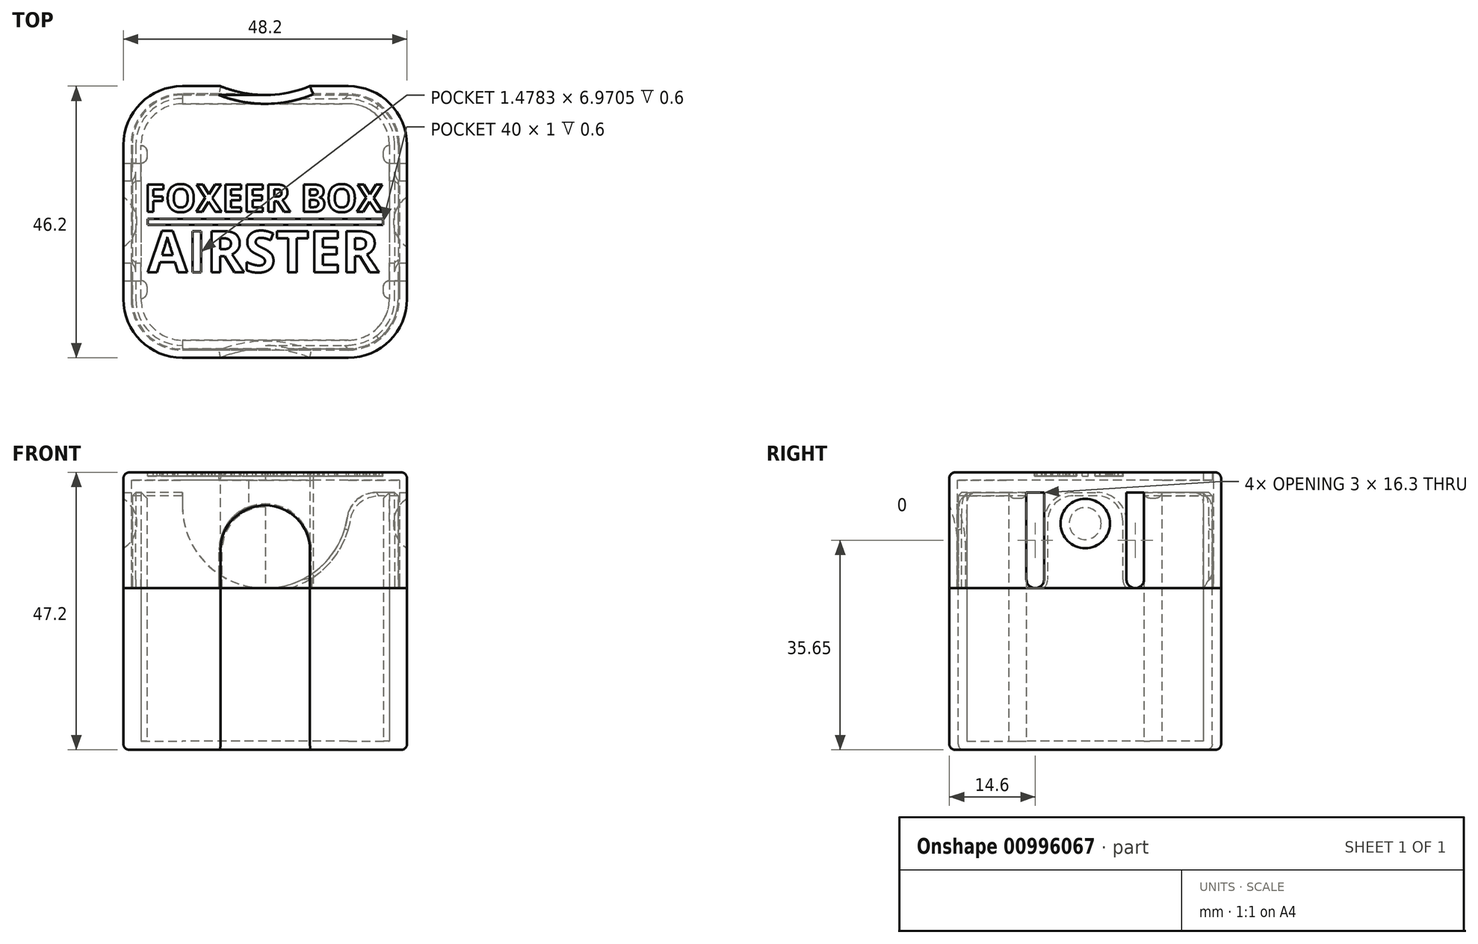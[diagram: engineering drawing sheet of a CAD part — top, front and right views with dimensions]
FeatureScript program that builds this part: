
annotation { "Feature Type Name" : "Feature", "Feature Type Description" : "" }
export const myFeature = defineFeature(function(context is Context, id is Id, definition is map)
    precondition{}
    {
        {
            var Q0;
            Q0=qCreatedBy(makeId("Top.planeOp"),FACE);
            var sketch = newSketch(context, id + "F0", { "sketchPlane" : qUnion([Q0])});
            skLineSegment(sketch, "E0.bottom", {"start": v(14.1, 20.1) * mm, "end": v(-14.1, 20.1) * mm});
            skLineSegment(sketch, "E0.top", {"start": v(14.1, -20.1) * mm, "end": v(-14.1, -20.1) * mm});
            skLineSegment(sketch, "E0.left", {"start": v(21.1, 13.1) * mm, "end": v(21.1, -13.1) * mm});
            skLineSegment(sketch, "E0.right", {"start": v(-21.1, 13.1) * mm, "end": v(-21.1, -13.1) * mm});
            skPoint(sketch, "E0.middle", {"position": v(0, 0) * mm});
            skPoint(sketch, "E1.visualSharp", {"position": v(-21.1, 20.1) * mm});
            skArc(sketch, "E1.filletArc", {"start": v(-14.1, 20.1) * mm, "mid": v(-19.05, 18.05) * mm, "end": v(-21.1, 13.1) * mm});
            skPoint(sketch, "E2.visualSharp", {"position": v(-21.1, -20.1) * mm});
            skArc(sketch, "E2.filletArc", {"start": v(-21.1, -13.1) * mm, "mid": v(-19.05, -18.05) * mm, "end": v(-14.1, -20.1) * mm});
            skPoint(sketch, "E3.visualSharp", {"position": v(21.1, -20.1) * mm});
            skArc(sketch, "E3.filletArc", {"start": v(14.1, -20.1) * mm, "mid": v(19.05, -18.05) * mm, "end": v(21.1, -13.1) * mm});
            skPoint(sketch, "E4.visualSharp", {"position": v(21.1, 20.1) * mm});
            skArc(sketch, "E4.filletArc", {"start": v(21.1, 13.1) * mm, "mid": v(19.05, 18.05) * mm, "end": v(14.1, 20.1) * mm});
            skArc(sketch, "E5.0", {"start": v(22.6, 13.1) * mm, "mid": v(20.11, 19.11) * mm, "end": v(14.1, 21.6) * mm});
            skLineSegment(sketch, "E5.1", {"start": v(14.1, 21.6) * mm, "end": v(-14.1, 21.6) * mm});
            skLineSegment(sketch, "E5.2", {"start": v(22.6, 13.1) * mm, "end": v(22.6, -13.1) * mm});
            skArc(sketch, "E5.3", {"start": v(-14.1, 21.6) * mm, "mid": v(-20.11, 19.11) * mm, "end": v(-22.6, 13.1) * mm});
            skArc(sketch, "E5.4", {"start": v(14.1, -21.6) * mm, "mid": v(20.11, -19.11) * mm, "end": v(22.6, -13.1) * mm});
            skLineSegment(sketch, "E5.5", {"start": v(14.1, -21.6) * mm, "end": v(-14.1, -21.6) * mm});
            skArc(sketch, "E5.6", {"start": v(-22.6, -13.1) * mm, "mid": v(-20.11, -19.11) * mm, "end": v(-14.1, -21.6) * mm});
            skLineSegment(sketch, "E5.7", {"start": v(-22.6, 13.1) * mm, "end": v(-22.6, -13.1) * mm});
            skLineSegment(sketch, "E6.0", {"start": v(24.1, 13.1) * mm, "end": v(24.1, -13.1) * mm});
            skArc(sketch, "E6.1", {"start": v(14.1, -23.1) * mm, "mid": v(21.17, -20.17) * mm, "end": v(24.1, -13.1) * mm});
            skArc(sketch, "E6.2", {"start": v(24.1, 13.1) * mm, "mid": v(21.17, 20.17) * mm, "end": v(14.1, 23.1) * mm});
            skLineSegment(sketch, "E6.3", {"start": v(14.1, -23.1) * mm, "end": v(-14.1, -23.1) * mm});
            skLineSegment(sketch, "E6.4", {"start": v(14.1, 23.1) * mm, "end": v(-14.1, 23.1) * mm});
            skArc(sketch, "E6.5", {"start": v(-14.1, 23.1) * mm, "mid": v(-21.17, 20.17) * mm, "end": v(-24.1, 13.1) * mm});
            skLineSegment(sketch, "E6.6", {"start": v(-24.1, 13.1) * mm, "end": v(-24.1, -13.1) * mm});
            skArc(sketch, "E6.7", {"start": v(-24.1, -13.1) * mm, "mid": v(-21.17, -20.17) * mm, "end": v(-14.1, -23.1) * mm});
            skLineSegment(sketch, "E7.bottom", {"start": v(-21.1, -13) * mm, "end": v(-20.1, -13) * mm});
            skLineSegment(sketch, "E7.top", {"start": v(-21.1, -10) * mm, "end": v(-20.1, -10) * mm});
            skLineSegment(sketch, "E7.left", {"start": v(-21.1, -13) * mm, "end": v(-21.1, -10) * mm});
            skLineSegment(sketch, "E7.right", {"start": v(-20.1, -13) * mm, "end": v(-20.1, -10) * mm});
            skLineSegment(sketch, "E8.MirrorCS", {"start": v(-20.1, 13) * mm, "end": v(-20.1, 10) * mm});
            skLineSegment(sketch, "E9.MirrorCS", {"start": v(-21.1, 10) * mm, "end": v(-20.1, 10) * mm});
            skLineSegment(sketch, "E10.MirrorCS", {"start": v(-21.1, 13) * mm, "end": v(-20.1, 13) * mm});
            skLineSegment(sketch, "E11.MirrorCS", {"start": v(21.1, 13) * mm, "end": v(20.1, 13) * mm});
            skLineSegment(sketch, "E12.MirrorCS", {"start": v(20.1, 13) * mm, "end": v(20.1, 10) * mm});
            skLineSegment(sketch, "E13.MirrorCS", {"start": v(21.1, 10) * mm, "end": v(20.1, 10) * mm});
            skLineSegment(sketch, "E14.MirrorCS", {"start": v(21.1, -10) * mm, "end": v(20.1, -10) * mm});
            skLineSegment(sketch, "E15.MirrorCS", {"start": v(20.1, -13) * mm, "end": v(20.1, -10) * mm});
            skLineSegment(sketch, "E16.MirrorCS", {"start": v(21.1, -13) * mm, "end": v(20.1, -13) * mm});
            skSolve(sketch);
        }
        {
            var Q0;
            Q0=makeQuery(id+"F0.imprint","IMPRINT",FACE,{"disambiguationData":[TD([[makeQuery(id+"F0.imprint","IMPRINT",EDGE,{"derivedFrom":sQuery(id+"F0.wireOp",EDGE,"E0.bottom")}),-1.0]])]});
            var Q1;
            Q1=makeQuery(id+"F0.imprint","IMPRINT",FACE,{"disambiguationData":[TD([[makeQuery(id+"F0.imprint","IMPRINT",EDGE,{"derivedFrom":sQuery(id+"F0.wireOp",EDGE,"E0.bottom")}),1.0]])]});
            var Q2;
            Q2=makeQuery(id+"F0.imprint","IMPRINT",FACE,{"disambiguationData":[TD([[makeQuery(id+"F0.imprint","IMPRINT",EDGE,{"derivedFrom":sQuery(id+"F0.wireOp",EDGE,"E5.0")}),-1.0]])]});
            var Q3;
            Q3=makeQuery(id+"F0.imprint","IMPRINT",FACE,{"disambiguationData":[TD([[makeQuery(id+"F0.imprint","IMPRINT",EDGE,{"derivedFrom":sQuery(id+"F0.wireOp",EDGE,"E5.0")}),1.0]])]});
            var Q4;
            Q4=makeQuery(id+"F0.imprint","IMPRINT",FACE,{"disambiguationData":[TD([[makeQuery(id+"F0.imprint","IMPRINT",EDGE,{"derivedFrom":sQuery(id+"F0.wireOp",EDGE,"E8.MirrorCS")}),-1.0]])]});
            var Q5;
            {var subQ0=sQuery(id+"F0.wireOp",EDGE,"E11.MirrorCS");Q5=makeQuery(id+"F0.imprint","IMPRINT",FACE,{"disambiguationData":[TD([[makeQuery(id+"F0.imprint","IMPRINT",EDGE,{"derivedFrom":subQ0}),1.0]])]});}
            var Q6;
            {var subQ0=sQuery(id+"F0.wireOp",EDGE,"E14.MirrorCS");Q6=makeQuery(id+"F0.imprint","IMPRINT",FACE,{"disambiguationData":[TD([[makeQuery(id+"F0.imprint","IMPRINT",EDGE,{"derivedFrom":subQ0}),1.0]])]});}
            var Q7;
            Q7=makeQuery(id+"F0.imprint","IMPRINT",FACE,{"disambiguationData":[TD([[makeQuery(id+"F0.imprint","IMPRINT",EDGE,{"derivedFrom":sQuery(id+"F0.wireOp",EDGE,"E7.bottom")}),1.0]])]});
            var Q8;
            {var subQ1=sQuery(id+"F0.wireOp",EDGE,"E7.top");Q8=makeQuery(id+"F0.imprint","IMPRINT",FACE,{"disambiguationData":[TD([[makeQuery(id+"F0.imprint","IMPRINT",EDGE,{"derivedFrom":subQ1}),-1.0]])]});}
            extrude(context, id + "F1", {"entities" : qUnion([Q0, Q1, Q2, Q3, Q4, Q5, Q6, Q7, Q8]), "oppositeDirection" : true, "depth" : 1.5 * mm, "offsetDistance" : 25 * mm});
        }
        {
            var Q0;
            Q0=makeQuery(id+"F0.imprint","IMPRINT",FACE,{"disambiguationData":[TD([[makeQuery(id+"F0.imprint","IMPRINT",EDGE,{"derivedFrom":sQuery(id+"F0.wireOp",EDGE,"E0.bottom")}),-1.0]])]});
            var Q1;
            Q1=makeQuery(id+"F0.imprint","IMPRINT",FACE,{"disambiguationData":[TD([[makeQuery(id+"F0.imprint","IMPRINT",EDGE,{"derivedFrom":sQuery(id+"F0.wireOp",EDGE,"E8.MirrorCS")}),-1.0]])]});
            var Q2;
            Q2=makeQuery(id+"F0.imprint","IMPRINT",FACE,{"disambiguationData":[TD([[makeQuery(id+"F0.imprint","IMPRINT",EDGE,{"derivedFrom":sQuery(id+"F0.wireOp",EDGE,"E7.bottom")}),1.0]])]});
            var Q3;
            {var subQ0=sQuery(id+"F0.wireOp",EDGE,"E11.MirrorCS");Q3=makeQuery(id+"F0.imprint","IMPRINT",FACE,{"disambiguationData":[TD([[makeQuery(id+"F0.imprint","IMPRINT",EDGE,{"derivedFrom":subQ0}),1.0]])]});}
            var Q4;
            {var subQ0=sQuery(id+"F0.wireOp",EDGE,"E14.MirrorCS");Q4=makeQuery(id+"F0.imprint","IMPRINT",FACE,{"disambiguationData":[TD([[makeQuery(id+"F0.imprint","IMPRINT",EDGE,{"derivedFrom":subQ0}),1.0]])]});}
            extrude(context, id + "F2", {"entities" : qUnion([Q0, Q1, Q2, Q3, Q4]), "operationType" : NewBodyOperationType.ADD, "depth" : 42.3 * mm, "offsetDistance" : 25 * mm});
        }
        {
            var Q0;
            Q0=makeQuery(id+"F0.imprint","IMPRINT",FACE,{"disambiguationData":[TD([[makeQuery(id+"F0.imprint","IMPRINT",EDGE,{"derivedFrom":sQuery(id+"F0.wireOp",EDGE,"E5.0")}),-1.0]])]});
            var Q1;
            Q1=makeQuery(id+"F0.imprint","IMPRINT",FACE,{"disambiguationData":[TD([[makeQuery(id+"F0.imprint","IMPRINT",EDGE,{"derivedFrom":sQuery(id+"F0.wireOp",EDGE,"E5.0")}),1.0]])]});
            extrude(context, id + "F3", {"entities" : qUnion([Q0, Q1]), "operationType" : NewBodyOperationType.ADD, "depth" : 26 * mm, "offsetDistance" : 25 * mm});
        }
        {
            var Q0;
            Q0=makeQuery(id+"F3.opExtrude","CAP_FACE",FACE,{"disambiguationData":[OSD([sQuery(id+"F0.wireOp",EDGE,"E0.bottom"),sQuery(id+"F0.wireOp",EDGE,"E0.top"),sQuery(id+"F0.wireOp",EDGE,"E0.left"),sQuery(id+"F0.wireOp",EDGE,"E0.right"),sQuery(id+"F0.wireOp",EDGE,"E1.filletArc"),sQuery(id+"F0.wireOp",EDGE,"E2.filletArc"),sQuery(id+"F0.wireOp",EDGE,"E3.filletArc"),sQuery(id+"F0.wireOp",EDGE,"E4.filletArc"),sQuery(id+"F0.wireOp",EDGE,"E6.0"),sQuery(id+"F0.wireOp",EDGE,"E6.1"),sQuery(id+"F0.wireOp",EDGE,"E6.2"),sQuery(id+"F0.wireOp",EDGE,"E6.3"),sQuery(id+"F0.wireOp",EDGE,"E6.4"),sQuery(id+"F0.wireOp",EDGE,"E6.5"),sQuery(id+"F0.wireOp",EDGE,"E6.6"),sQuery(id+"F0.wireOp",EDGE,"E6.7")])],"isStart":false});
            var sketch = newSketch(context, id + "F4", { "sketchPlane" : qUnion([Q0])});
            skSolve(sketch);
        }
        {
            var Q0;
            Q0=makeQuery(id+"F2.opExtrude","SWEPT_FACE",FACE,{"disambiguationData":[OSD([sQuery(id+"F0.wireOp",EDGE,"E5.5")])]});
            var sketch = newSketch(context, id + "F5", { "sketchPlane" : qUnion([Q0])});
            skArc(sketch, "E17", {"start": v(-14.1, 40.1) * mm, "mid": v(0, 26) * mm, "end": v(14.1, 40.1) * mm});
            skSolve(sketch);
        }
        {
            var Q0;
            {var subQ0=sQuery(id+"F0.wireOp",EDGE,"E5.5");var subQ2=makeQuery(id+"F2.opExtrude","CAP_EDGE",EDGE,{"disambiguationData":[OSD([subQ0])],"isStart":false});Q0=makeQuery(id+"F5.imprint","IMPRINT",FACE,{"disambiguationData":[TD([[makeQuery(id+"F5.imprint","IMPRINT",EDGE,{"derivedFrom":subQ2}),1.0]])]});}
            extrude(context, id + "F6", {"entities" : qUnion([Q0]), "operationType" : NewBodyOperationType.REMOVE, "endBound" : BoundingType.THROUGH_ALL, "oppositeDirection" : true, "depth" : 25 * mm, "offsetDistance" : 25 * mm});
        }
        {
            var Q0;
            {var subQ0=sQuery(id+"F0.wireOp",EDGE,"E5.6");var subQ1=sQuery(id+"F0.wireOp",EDGE,"E5.5");var subQ2=sQuery(id+"F0.wireOp",EDGE,"E2.filletArc");Q0=makeQuery(id+"F6.boolean.opBoolean","COPY",EDGE,{"disambiguationData":[TD([makeQuery(id+"F2.opExtrude","SWEPT_FACE",FACE,{"disambiguationData":[OSD([subQ2])]})])],"derivedFrom":makeQuery(id+"F6.opExtrude","SWEPT_EDGE",EDGE,{"disambiguationData":[OSD([subQ1,subQ0])]})});}
            var Q1;
            {var subQ0=sQuery(id+"F0.wireOp",EDGE,"E5.5");var subQ1=sQuery(id+"F0.wireOp",EDGE,"E5.4");var subQ2=sQuery(id+"F0.wireOp",EDGE,"E3.filletArc");Q1=makeQuery(id+"F6.boolean.opBoolean","COPY",EDGE,{"disambiguationData":[TD([makeQuery(id+"F2.opExtrude","SWEPT_FACE",FACE,{"disambiguationData":[OSD([subQ2])]})])],"derivedFrom":makeQuery(id+"F6.opExtrude","SWEPT_EDGE",EDGE,{"disambiguationData":[OSD([subQ1,subQ0])]})});}
            var Q2;
            {var subQ0=sQuery(id+"F0.wireOp",EDGE,"E5.5");var subQ1=sQuery(id+"F0.wireOp",EDGE,"E5.4");var subQ3=sQuery(id+"F0.wireOp",EDGE,"E4.filletArc");Q2=makeQuery(id+"F6.boolean.opBoolean","COPY",EDGE,{"disambiguationData":[TD([makeQuery(id+"F2.opExtrude","SWEPT_FACE",FACE,{"disambiguationData":[OSD([subQ3])]})])],"derivedFrom":makeQuery(id+"F6.opExtrude","SWEPT_EDGE",EDGE,{"disambiguationData":[OSD([subQ1,subQ0])]})});}
            var Q3;
            {var subQ0=sQuery(id+"F0.wireOp",EDGE,"E5.6");var subQ1=sQuery(id+"F0.wireOp",EDGE,"E5.5");var subQ3=sQuery(id+"F0.wireOp",EDGE,"E1.filletArc");Q3=makeQuery(id+"F6.boolean.opBoolean","COPY",EDGE,{"disambiguationData":[TD([makeQuery(id+"F2.opExtrude","SWEPT_FACE",FACE,{"disambiguationData":[OSD([subQ3])]})])],"derivedFrom":makeQuery(id+"F6.opExtrude","SWEPT_EDGE",EDGE,{"disambiguationData":[OSD([subQ1,subQ0])]})});}
            fillet(context, id + "F7", {"entities" : qUnion([Q0, Q1, Q2, Q3]), "radius" : 5 * mm, "tangentPropagation" : true, "allowEdgeOverflow" : false});
        }
        {
            var Q0;
            Q0=makeQuery(id+"F2.opExtrude","SWEPT_EDGE",EDGE,{"disambiguationData":[OSD([sQuery(id+"F0.wireOp",EDGE,"E8.MirrorCS"),sQuery(id+"F0.wireOp",EDGE,"E9.MirrorCS")])]});
            var Q1;
            Q1=makeQuery(id+"F2.opExtrude","SWEPT_EDGE",EDGE,{"disambiguationData":[OSD([sQuery(id+"F0.wireOp",EDGE,"E8.MirrorCS"),sQuery(id+"F0.wireOp",EDGE,"E10.MirrorCS")])]});
            var Q2;
            Q2=makeQuery(id+"F2.opExtrude","SWEPT_EDGE",EDGE,{"disambiguationData":[OSD([sQuery(id+"F0.wireOp",EDGE,"E7.bottom"),sQuery(id+"F0.wireOp",EDGE,"E7.right")])]});
            var Q3;
            Q3=makeQuery(id+"F2.opExtrude","SWEPT_EDGE",EDGE,{"disambiguationData":[OSD([sQuery(id+"F0.wireOp",EDGE,"E7.top"),sQuery(id+"F0.wireOp",EDGE,"E7.right")])]});
            var Q4;
            Q4=makeQuery(id+"F2.opExtrude","SWEPT_EDGE",EDGE,{"disambiguationData":[OSD([sQuery(id+"F0.wireOp",EDGE,"E12.MirrorCS"),sQuery(id+"F0.wireOp",EDGE,"E13.MirrorCS")])]});
            var Q5;
            Q5=makeQuery(id+"F2.opExtrude","SWEPT_EDGE",EDGE,{"disambiguationData":[OSD([sQuery(id+"F0.wireOp",EDGE,"E14.MirrorCS"),sQuery(id+"F0.wireOp",EDGE,"E15.MirrorCS")])]});
            var Q6;
            Q6=makeQuery(id+"F2.opExtrude","SWEPT_EDGE",EDGE,{"disambiguationData":[OSD([sQuery(id+"F0.wireOp",EDGE,"E15.MirrorCS"),sQuery(id+"F0.wireOp",EDGE,"E16.MirrorCS")])]});
            var Q7;
            Q7=makeQuery(id+"F2.opExtrude","SWEPT_EDGE",EDGE,{"disambiguationData":[OSD([sQuery(id+"F0.wireOp",EDGE,"E11.MirrorCS"),sQuery(id+"F0.wireOp",EDGE,"E12.MirrorCS")])]});
            fillet(context, id + "F8", {"entities" : qUnion([Q0, Q1, Q2, Q3, Q4, Q5, Q6, Q7]), "radius" : 1 * mm, "tangentPropagation" : true, "allowEdgeOverflow" : false});
        }
        {
            var Q0;
            {var subQ7=sQuery(id+"F0.wireOp",EDGE,"E6.0");Q0=makeQuery(id+"F4.imprint","IMPRINT",FACE,{"disambiguationData":[TD([[makeQuery(id+"F4.imprint","IMPRINT",EDGE,{"derivedFrom":makeQuery(id+"F3.opExtrude","CAP_EDGE",EDGE,{"disambiguationData":[OSD([subQ7])],"isStart":false})}),-1.0]])]});}
            var Q1;
            {var subQ0=makeQuery(id+"F3.opExtrude","CAP_FACE",FACE,{"disambiguationData":[OSD([sQuery(id+"F0.wireOp",EDGE,"E0.bottom"),sQuery(id+"F0.wireOp",EDGE,"E0.top"),sQuery(id+"F0.wireOp",EDGE,"E0.left"),sQuery(id+"F0.wireOp",EDGE,"E0.right"),sQuery(id+"F0.wireOp",EDGE,"E1.filletArc"),sQuery(id+"F0.wireOp",EDGE,"E2.filletArc"),sQuery(id+"F0.wireOp",EDGE,"E3.filletArc"),sQuery(id+"F0.wireOp",EDGE,"E4.filletArc"),sQuery(id+"F0.wireOp",EDGE,"E6.0"),sQuery(id+"F0.wireOp",EDGE,"E6.1"),sQuery(id+"F0.wireOp",EDGE,"E6.2"),sQuery(id+"F0.wireOp",EDGE,"E6.3"),sQuery(id+"F0.wireOp",EDGE,"E6.4"),sQuery(id+"F0.wireOp",EDGE,"E6.5"),sQuery(id+"F0.wireOp",EDGE,"E6.6"),sQuery(id+"F0.wireOp",EDGE,"E6.7")])],"isStart":false});Q1=makeQuery(id+"F4.imprint","IMPRINT",FACE,{"disambiguationData":[TD([[makeQuery(id+"F4.imprint","IMPRINT",EDGE,{"derivedFrom":makeQuery(id+"F3.boolean.opBoolean","INTERSECT",EDGE,{"derivedFrom":[makeQuery(id+"F2.opExtrude","SWEPT_FACE",FACE,{"disambiguationData":[OSD([sQuery(id+"F0.wireOp",EDGE,"E5.0")])]}),subQ0]})}),1.0]])]});}
            var Q2;
            {var subQ0=sQuery(id+"F0.wireOp",EDGE,"760bae26-e821-4f93-9cbd-1cc9cc26cd04.2");var subQ1=sQuery(id+"F0.wireOp",EDGE,"E2.filletArc");var subQ2=sQuery(id+"F0.wireOp",EDGE,"E1.filletArc");var subQ3=sQuery(id+"F0.wireOp",EDGE,"E0.right");var subQ4=sQuery(id+"F0.wireOp",EDGE,"760bae26-e821-4f93-9cbd-1cc9cc26cd04.4");var subQ5=sQuery(id+"F0.wireOp",EDGE,"760bae26-e821-4f93-9cbd-1cc9cc26cd04.6");var subQ6=sQuery(id+"F0.wireOp",EDGE,"760bae26-e821-4f93-9cbd-1cc9cc26cd04.5");Q2=makeQuery(id+"F6.boolean.opBoolean","SPLIT",FACE,{"disambiguationData":[TD([makeQuery(id+"F2.opExtrude","SWEPT_FACE",FACE,{"disambiguationData":[OSD([subQ3])]})])],"derivedFrom":makeQuery(id+"F2.opExtrude","CAP_FACE",FACE,{"disambiguationData":[OSD([sQuery(id+"F0.wireOp",EDGE,"E0.bottom"),sQuery(id+"F0.wireOp",EDGE,"E0.top"),sQuery(id+"F0.wireOp",EDGE,"E0.left"),subQ3,subQ2,subQ1,sQuery(id+"F0.wireOp",EDGE,"E3.filletArc"),sQuery(id+"F0.wireOp",EDGE,"E4.filletArc"),sQuery(id+"F0.wireOp",EDGE,"760bae26-e821-4f93-9cbd-1cc9cc26cd04.0"),sQuery(id+"F0.wireOp",EDGE,"760bae26-e821-4f93-9cbd-1cc9cc26cd04.1"),subQ0,sQuery(id+"F0.wireOp",EDGE,"760bae26-e821-4f93-9cbd-1cc9cc26cd04.3"),subQ4,subQ6,subQ5,sQuery(id+"F0.wireOp",EDGE,"760bae26-e821-4f93-9cbd-1cc9cc26cd04.7")])],"isStart":false})});}
            extrude(context, id + "F9", {"entities" : qUnion([Q0, Q1]), "depth" : 19.7 * mm, "endBoundEntityFace" : qUnion([Q2]), "hasOffset" : true, "offsetDistance" : -1.5 * mm});
        }
        {
            var Q0;
            Q0=makeQuery(id+"F9.opExtrude","SWEPT_FACE",FACE,{"disambiguationData":[OSD([sQuery(id+"F0.wireOp",EDGE,"E6.3")])]});
            cPlane(context, id + "F10", {"entities" : qUnion([Q0]), "cplaneType" : CPlaneType.OFFSET, "offset" : 18.5 * mm, "width" : 150 * mm, "height" : 150 * mm});
        }
        {
            var Q0;
            Q0=qCreatedBy(id+"F10.planeOp",FACE);
            var sketch = newSketch(context, id + "F11", { "sketchPlane" : qUnion([Q0])});
            skArc(sketch, "E18", {"start": v(0, 12.5) * mm, "mid": v(20, 32.5) * mm, "end": v(0, 52.5) * mm});
            skLineSegment(sketch, "E19", {"start": v(0, 52.5) * mm, "end": v(0, 12.5) * mm});
            skLineSegment(sketch, "E20", {"start": v(0, 32.5) * mm, "end": v(20, 32.5) * mm});
            skSolve(sketch);
        }
        {
            var Q0;
            {var subQ3=sQuery(id+"F11.wireOp",EDGE,"E20");Q0=makeQuery(id+"F11.imprint","IMPRINT",FACE,{"disambiguationData":[TD([[makeQuery(id+"F11.imprint","IMPRINT",EDGE,{"derivedFrom":subQ3}),1.0]])]});}
            var Q1;
            Q1=sQuery(id+"F11.wireOp",EDGE,"E19");
            revolve(context, id + "F12", {"entities" : qUnion([Q0]), "axis" : qUnion([Q1]), "revolveType" : RevolveType.ONE_DIRECTION, "oppositeDirection" : true, "angle" : 180 * degree});
        }
        {
            var Q0;
            Q0=makeQuery(id+"F12.opRevolve","SWEPT_BODY",BODY,{"disambiguationData":[OSD([sQuery(id+"F11.wireOp",EDGE,"E18"),sQuery(id+"F11.wireOp",EDGE,"E19")])]});
            var Q1;
            Q1=qCreatedBy(makeId("Front.planeOp"),FACE);
            mirror(context, id + "F13", {"entities" : qUnion([Q0]), "mirrorPlane" : qUnion([Q1])});
        }
        {
            var Q0;
            Q0=makeQuery(id+"F13.opPattern","COPY",BODY,{"derivedFrom":makeQuery(id+"F12.opRevolve","SWEPT_BODY",BODY,{"disambiguationData":[OSD([sQuery(id+"F11.wireOp",EDGE,"E18"),sQuery(id+"F11.wireOp",EDGE,"E19")])]}),"instanceName":"1"});
            var Q1;
            Q1=makeQuery(id+"F12.opRevolve","SWEPT_BODY",BODY,{"disambiguationData":[OSD([sQuery(id+"F11.wireOp",EDGE,"E18"),sQuery(id+"F11.wireOp",EDGE,"E19")])]});
            var Q2;
            Q2=makeQuery(id+"F9.opExtrude","SWEPT_BODY",BODY,{"disambiguationData":[OSD([sQuery(id+"F0.wireOp",EDGE,"E6.0"),sQuery(id+"F0.wireOp",EDGE,"E6.1"),sQuery(id+"F0.wireOp",EDGE,"E6.2"),sQuery(id+"F0.wireOp",EDGE,"E6.3"),sQuery(id+"F0.wireOp",EDGE,"E6.4"),sQuery(id+"F0.wireOp",EDGE,"E6.5"),sQuery(id+"F0.wireOp",EDGE,"E6.6"),sQuery(id+"F0.wireOp",EDGE,"E6.7")])]});
            var Q3;
            Q3=makeQuery(id+"F1.opExtrude","SWEPT_BODY",BODY,{"disambiguationData":[OSD([sQuery(id+"F0.wireOp",EDGE,"E6.0"),sQuery(id+"F0.wireOp",EDGE,"E6.1"),sQuery(id+"F0.wireOp",EDGE,"E6.2"),sQuery(id+"F0.wireOp",EDGE,"E6.3"),sQuery(id+"F0.wireOp",EDGE,"E6.4"),sQuery(id+"F0.wireOp",EDGE,"E6.5"),sQuery(id+"F0.wireOp",EDGE,"E6.6"),sQuery(id+"F0.wireOp",EDGE,"E6.7")])]});
            booleanBodies(context, id + "F14", {"operationType" : BooleanOperationType.SUBTRACTION, "tools" : qUnion([Q0, Q1]), "targets" : qUnion([Q2, Q3])});
        }
        {
            var Q0;
            Q0=makeQuery(id+"F14.opBoolean","COPY",FACE,{"derivedFrom":makeQuery(id+"F12.opRevolve","SWEPT_FACE",FACE,{"disambiguationData":[OSD([sQuery(id+"F11.wireOp",EDGE,"E20")])]})});
            var Q1;
            Q1=makeQuery(id+"F14.opBoolean","COPY",FACE,{"derivedFrom":makeQuery(id+"F13.opPattern","COPY",FACE,{"derivedFrom":makeQuery(id+"F12.opRevolve","SWEPT_FACE",FACE,{"disambiguationData":[OSD([sQuery(id+"F11.wireOp",EDGE,"E20")])]}),"instanceName":"1"})});
            extrude(context, id + "F15", {"entities" : qUnion([Q0, Q1]), "operationType" : NewBodyOperationType.REMOVE, "endBound" : BoundingType.THROUGH_ALL, "oppositeDirection" : true, "depth" : 25 * mm, "offsetDistance" : 25 * mm});
        }
        {
            var Q0;
            {var subQ0=sQuery(id+"F11.wireOp",EDGE,"E20");var subQ1=sQuery(id+"F11.wireOp",EDGE,"E18");Q0=makeQuery(id+"F15.boolean.opBoolean","INTERSECT",EDGE,{"derivedFrom":[makeQuery(id+"F1.opExtrude","CAP_FACE",FACE,{"disambiguationData":[OSD([sQuery(id+"F0.wireOp",EDGE,"E6.0"),sQuery(id+"F0.wireOp",EDGE,"E6.1"),sQuery(id+"F0.wireOp",EDGE,"E6.2"),sQuery(id+"F0.wireOp",EDGE,"E6.3"),sQuery(id+"F0.wireOp",EDGE,"E6.4"),sQuery(id+"F0.wireOp",EDGE,"E6.5"),sQuery(id+"F0.wireOp",EDGE,"E6.6"),sQuery(id+"F0.wireOp",EDGE,"E6.7")])],"isStart":false}),makeQuery(id+"F15.opExtrude","SWEPT_FACE",FACE,{"disambiguationData":[OSD([subQ1,subQ0]),TDD([makeQuery(id+"F14.opBoolean","COPY",EDGE,{"derivedFrom":makeQuery(id+"F12.opRevolve","SWEPT_EDGE",EDGE,{"disambiguationData":[OSD([subQ1,subQ0])]})})])]})]});}
            var Q1;
            Q1=makeQuery(id+"F1.opExtrude","CAP_EDGE",EDGE,{"disambiguationData":[OSD([sQuery(id+"F0.wireOp",EDGE,"E6.0")])],"isStart":false});
            var Q2;
            Q2=makeQuery(id+"F1.opExtrude","CAP_EDGE",EDGE,{"disambiguationData":[OSD([sQuery(id+"F0.wireOp",EDGE,"E6.6")])],"isStart":false});
            var Q3;
            {var subQ0=sQuery(id+"F11.wireOp",EDGE,"E20");var subQ1=sQuery(id+"F11.wireOp",EDGE,"E18");Q3=makeQuery(id+"F15.boolean.opBoolean","INTERSECT",EDGE,{"derivedFrom":[makeQuery(id+"F1.opExtrude","CAP_FACE",FACE,{"disambiguationData":[OSD([sQuery(id+"F0.wireOp",EDGE,"E6.0"),sQuery(id+"F0.wireOp",EDGE,"E6.1"),sQuery(id+"F0.wireOp",EDGE,"E6.2"),sQuery(id+"F0.wireOp",EDGE,"E6.3"),sQuery(id+"F0.wireOp",EDGE,"E6.4"),sQuery(id+"F0.wireOp",EDGE,"E6.5"),sQuery(id+"F0.wireOp",EDGE,"E6.6"),sQuery(id+"F0.wireOp",EDGE,"E6.7")])],"isStart":false}),makeQuery(id+"F15.opExtrude","SWEPT_FACE",FACE,{"disambiguationData":[OSD([subQ1,subQ0]),TDD([makeQuery(id+"F14.opBoolean","COPY",EDGE,{"derivedFrom":makeQuery(id+"F13.opPattern","COPY",EDGE,{"derivedFrom":makeQuery(id+"F12.opRevolve","SWEPT_EDGE",EDGE,{"disambiguationData":[OSD([subQ1,subQ0])]}),"instanceName":"1"})})])]})]});}
            fillet(context, id + "F16", {"entities" : qUnion([Q0, Q1, Q2, Q3]), "radius" : 1 * mm, "tangentPropagation" : true, "allowEdgeOverflow" : false});
        }
        {
            var Q0;
            Q0=makeQuery(id+"F9.opExtrude","CAP_FACE",FACE,{"disambiguationData":[OSD([sQuery(id+"F0.wireOp",EDGE,"E6.0"),sQuery(id+"F0.wireOp",EDGE,"E6.1"),sQuery(id+"F0.wireOp",EDGE,"E6.2"),sQuery(id+"F0.wireOp",EDGE,"E6.3"),sQuery(id+"F0.wireOp",EDGE,"E6.4"),sQuery(id+"F0.wireOp",EDGE,"E6.5"),sQuery(id+"F0.wireOp",EDGE,"E6.6"),sQuery(id+"F0.wireOp",EDGE,"E6.7")])],"isStart":true});
            shell(context, id + "F17", {"entities" : qUnion([Q0]), "thickness" : 1.3 * mm});
        }
        {
            var Q0;
            Q0=makeQuery(id+"F9.opExtrude","SWEPT_FACE",FACE,{"disambiguationData":[OSD([sQuery(id+"F0.wireOp",EDGE,"E6.0")])]});
            cPlane(context, id + "F18", {"entities" : qUnion([Q0]), "cplaneType" : CPlaneType.OFFSET, "offset" : 2.7 * mm, "width" : 150 * mm, "height" : 150 * mm});
        }
        {
            var Q0;
            Q0=qCreatedBy(id+"F18.planeOp",FACE);
            var sketch = newSketch(context, id + "F19", { "sketchPlane" : qUnion([Q0])});
            skArc(sketch, "E21", {"start": v(0, 32) * mm, "mid": v(5, 37) * mm, "end": v(0, 42) * mm});
            skLineSegment(sketch, "E22", {"start": v(0, 42) * mm, "end": v(0, 32) * mm});
            skLineSegment(sketch, "E23.bottom", {"start": v(-10, 42.3) * mm, "end": v(-7, 42.3) * mm});
            skLineSegment(sketch, "E23.top", {"start": v(-8.5, 26) * mm, "end": v(-8.5, 26) * mm});
            skLineSegment(sketch, "E23.left", {"start": v(-10, 42.3) * mm, "end": v(-10, 27.5) * mm});
            skLineSegment(sketch, "E23.right", {"start": v(-7, 42.3) * mm, "end": v(-7, 27.5) * mm});
            skLineSegment(sketch, "E24.MirrorCS", {"start": v(7, 42.3) * mm, "end": v(7, 27.5) * mm});
            skLineSegment(sketch, "E25.MirrorCS", {"start": v(10, 42.3) * mm, "end": v(10, 27.5) * mm});
            skLineSegment(sketch, "E26.MirrorCS", {"start": v(10, 42.3) * mm, "end": v(7, 42.3) * mm});
            skLineSegment(sketch, "E27.MirrorCS", {"start": v(8.5, 26) * mm, "end": v(8.5, 26) * mm});
            skPoint(sketch, "E28.visualSharp", {"position": v(-10, 26) * mm});
            skArc(sketch, "E28.filletArc", {"start": v(-10, 27.5) * mm, "mid": v(-9.56, 26.44) * mm, "end": v(-8.5, 26) * mm});
            skPoint(sketch, "E29.visualSharp", {"position": v(-7, 26) * mm});
            skArc(sketch, "E29.filletArc", {"start": v(-8.5, 26) * mm, "mid": v(-7.44, 26.44) * mm, "end": v(-7, 27.5) * mm});
            skPoint(sketch, "E30.visualSharp", {"position": v(7, 26) * mm});
            skArc(sketch, "E30.filletArc", {"start": v(7, 27.5) * mm, "mid": v(7.44, 26.44) * mm, "end": v(8.5, 26) * mm});
            skPoint(sketch, "E31.visualSharp", {"position": v(10, 26) * mm});
            skArc(sketch, "E31.filletArc", {"start": v(8.5, 26) * mm, "mid": v(9.56, 26.44) * mm, "end": v(10, 27.5) * mm});
            skSolve(sketch);
        }
        {
            var Q0;
            Q0=makeQuery(id+"F19.imprint","IMPRINT",FACE,{"disambiguationData":[TD([[makeQuery(id+"F19.imprint","IMPRINT",EDGE,{"derivedFrom":sQuery(id+"F19.wireOp",EDGE,"E21")}),1.0]])]});
            var Q1;
            Q1=sQuery(id+"F19.wireOp",EDGE,"E22");
            revolve(context, id + "F20", {"entities" : qUnion([Q0]), "axis" : qUnion([Q1]), "revolveType" : RevolveType.ONE_DIRECTION, "oppositeDirection" : true, "angle" : 180 * degree});
        }
        {
            var Q0;
            Q0=makeQuery(id+"F20.opRevolve","SWEPT_BODY",BODY,{"disambiguationData":[OSD([sQuery(id+"F19.wireOp",EDGE,"E21"),sQuery(id+"F19.wireOp",EDGE,"E22")])]});
            var Q1;
            Q1=qCreatedBy(makeId("Right.planeOp"),FACE);
            mirror(context, id + "F21", {"entities" : qUnion([Q0]), "mirrorPlane" : qUnion([Q1])});
        }
        {
            var Q0;
            Q0=makeQuery(id+"F21.opPattern","COPY",BODY,{"derivedFrom":makeQuery(id+"F20.opRevolve","SWEPT_BODY",BODY,{"disambiguationData":[OSD([sQuery(id+"F19.wireOp",EDGE,"E21"),sQuery(id+"F19.wireOp",EDGE,"E22")])]}),"instanceName":"1"});
            var Q1;
            Q1=makeQuery(id+"F20.opRevolve","SWEPT_BODY",BODY,{"disambiguationData":[OSD([sQuery(id+"F19.wireOp",EDGE,"E21"),sQuery(id+"F19.wireOp",EDGE,"E22")])]});
            var Q2;
            Q2=makeQuery(id+"F1.opExtrude","SWEPT_BODY",BODY,{"disambiguationData":[OSD([sQuery(id+"F0.wireOp",EDGE,"E6.0"),sQuery(id+"F0.wireOp",EDGE,"E6.1"),sQuery(id+"F0.wireOp",EDGE,"E6.2"),sQuery(id+"F0.wireOp",EDGE,"E6.3"),sQuery(id+"F0.wireOp",EDGE,"E6.4"),sQuery(id+"F0.wireOp",EDGE,"E6.5"),sQuery(id+"F0.wireOp",EDGE,"E6.6"),sQuery(id+"F0.wireOp",EDGE,"E6.7")])]});
            booleanBodies(context, id + "F22", {"operationType" : BooleanOperationType.SUBTRACTION, "tools" : qUnion([Q0, Q1]), "targets" : qUnion([Q2]), "keepTools" : true});
        }
        {
            var Q0;
            Q0=makeQuery(id+"F21.opPattern","COPY",FACE,{"derivedFrom":makeQuery(id+"F20.opRevolve","CAP_FACE",FACE,{"disambiguationData":[OSD([sQuery(id+"F19.wireOp",EDGE,"E21"),sQuery(id+"F19.wireOp",EDGE,"E22")])],"isStart":true}),"instanceName":"1"});
            var Q1;
            Q1=makeQuery(id+"F9.opExtrude","SWEPT_FACE",FACE,{"disambiguationData":[OSD([sQuery(id+"F0.wireOp",EDGE,"E6.6")])]});
            extrude(context, id + "F23", {"entities" : qUnion([Q0]), "operationType" : NewBodyOperationType.REMOVE, "endBound" : BoundingType.UP_TO_SURFACE, "oppositeDirection" : true, "depth" : 25 * mm, "endBoundEntityFace" : qUnion([Q1]), "offsetDistance" : 25 * mm});
        }
        {
            var Q0;
            Q0=makeQuery(id+"F20.opRevolve","CAP_FACE",FACE,{"disambiguationData":[OSD([sQuery(id+"F19.wireOp",EDGE,"E21"),sQuery(id+"F19.wireOp",EDGE,"E22")])],"isStart":true});
            var Q1;
            Q1=makeQuery(id+"F9.opExtrude","SWEPT_FACE",FACE,{"disambiguationData":[OSD([sQuery(id+"F0.wireOp",EDGE,"E6.0")])]});
            extrude(context, id + "F24", {"entities" : qUnion([Q0]), "operationType" : NewBodyOperationType.REMOVE, "endBound" : BoundingType.UP_TO_SURFACE, "oppositeDirection" : true, "depth" : 25 * mm, "endBoundEntityFace" : qUnion([Q1]), "offsetDistance" : 25 * mm});
        }
        {
            var Q0;
            {var subQ0=sQuery(id+"F4.wireOp",EDGE,"85f63282-6bf9-4db7-9a1d-20234ae27612.7");var subQ1=sQuery(id+"F4.wireOp",EDGE,"85f63282-6bf9-4db7-9a1d-20234ae27612.6");var subQ2=sQuery(id+"F4.wireOp",EDGE,"85f63282-6bf9-4db7-9a1d-20234ae27612.5");var subQ3=sQuery(id+"F4.wireOp",EDGE,"85f63282-6bf9-4db7-9a1d-20234ae27612.4");var subQ4=sQuery(id+"F4.wireOp",EDGE,"85f63282-6bf9-4db7-9a1d-20234ae27612.3");var subQ5=sQuery(id+"F4.wireOp",EDGE,"85f63282-6bf9-4db7-9a1d-20234ae27612.2");var subQ6=sQuery(id+"F4.wireOp",EDGE,"85f63282-6bf9-4db7-9a1d-20234ae27612.1");var subQ7=sQuery(id+"F4.wireOp",EDGE,"85f63282-6bf9-4db7-9a1d-20234ae27612.0");Q0=makeQuery(id+"FcbCElI8lbq80RP_2.boolean.opBoolean","MERGE",FACE,{"derivedFrom":[makeQuery(id+"F9.opExtrude","CAP_FACE",FACE,{"disambiguationData":[OSD([sQuery(id+"F0.wireOp",EDGE,"E6.0"),sQuery(id+"F0.wireOp",EDGE,"E6.1"),sQuery(id+"F0.wireOp",EDGE,"E6.2"),sQuery(id+"F0.wireOp",EDGE,"E6.3"),sQuery(id+"F0.wireOp",EDGE,"E6.4"),sQuery(id+"F0.wireOp",EDGE,"E6.5"),sQuery(id+"F0.wireOp",EDGE,"E6.6"),sQuery(id+"F0.wireOp",EDGE,"E6.7"),subQ7,subQ6,subQ5,subQ4,subQ3,subQ2,subQ1,subQ0])],"isStart":false}),makeQuery(id+"FcbCElI8lbq80RP_2.opExtrude","CAP_FACE",FACE,{"disambiguationData":[OSD([subQ7,subQ6,subQ5,subQ4,subQ3,subQ2,subQ1,subQ0])],"isStart":true})]});}
            var sketch = newSketch(context, id + "F25", { "sketchPlane" : qUnion([Q0])});
            skText(sketch, "E32", { "text": "AIRSTER", "fontName": "OpenSans-Bold.ttf"});
            skLineSegment(sketch, "E33.bottom", {"start": v(-20, -0.5) * mm, "end": v(20, -0.5) * mm});
            skLineSegment(sketch, "E33.top", {"start": v(-20, 0.5) * mm, "end": v(20, 0.5) * mm});
            skLineSegment(sketch, "E33.left", {"start": v(-20, -0.5) * mm, "end": v(-20, 0.5) * mm});
            skLineSegment(sketch, "E33.right", {"start": v(20, -0.5) * mm, "end": v(20, 0.5) * mm});
            skPoint(sketch, "E33.middle", {"position": v(0, 0) * mm});
            skText(sketch, "E34", { "text": "FOXEER BOX", "fontName": "OpenSans-Bold.ttf"});
            const initialGuessF25  = {"E32": [-0.02, -0.00853, 1, 0, 0.00703], "E34": [-0.02057, 0.0017, 1, 0, 0.00472]};
            skSetInitialGuess(sketch, initialGuessF25);
            skSolve(sketch);
        }
        {
            var Q0;
            Q0=qSketchRegion(id+"F25",true);
            extrude(context, id + "F26", {"entities" : qUnion([Q0]), "operationType" : NewBodyOperationType.REMOVE, "oppositeDirection" : true, "depth" : 0.6 * mm, "offsetDistance" : 25 * mm});
        }
        {
            var Q0;
            Q0=makeQuery(id+"F9.opExtrude","CAP_EDGE",EDGE,{"disambiguationData":[OSD([sQuery(id+"F0.wireOp",EDGE,"E6.0")])],"isStart":false});
            fillet(context, id + "F27", {"entities" : qUnion([Q0]), "radius" : 1 * mm, "tangentPropagation" : true, "allowEdgeOverflow" : false});
        }
        {
            var Q0;
            Q0=makeQuery(id+"F19.imprint","IMPRINT",FACE,{"disambiguationData":[TD([[makeQuery(id+"F19.imprint","IMPRINT",EDGE,{"derivedFrom":sQuery(id+"F19.wireOp",EDGE,"E23.bottom")}),-1.0]])]});
            var Q1;
            Q1=makeQuery(id+"F19.imprint","IMPRINT",FACE,{"disambiguationData":[TD([[makeQuery(id+"F19.imprint","IMPRINT",EDGE,{"derivedFrom":sQuery(id+"F19.wireOp",EDGE,"E24.MirrorCS")}),1.0]])]});
            extrude(context, id + "F28", {"entities" : qUnion([Q0, Q1]), "operationType" : NewBodyOperationType.REMOVE, "endBound" : BoundingType.THROUGH_ALL, "oppositeDirection" : true, "depth" : 25 * mm, "offsetDistance" : 25 * mm});
        }
        {
            var Q0;
            {var subQ1=sQuery(id+"F0.wireOp",EDGE,"E0.left");var subQ2=sQuery(id+"F19.wireOp",EDGE,"E23.left");Q0=makeQuery(id+"F28.boolean.opBoolean","COPY",EDGE,{"disambiguationData":[TD([makeQuery(id+"F2.opExtrude","SWEPT_FACE",FACE,{"disambiguationData":[OSD([subQ1])]})])],"derivedFrom":makeQuery(id+"F28.opExtrude","SWEPT_EDGE",EDGE,{"disambiguationData":[OSD([sQuery(id+"F19.wireOp",EDGE,"E23.bottom"),subQ2])]})});}
            var Q1;
            {var subQ1=sQuery(id+"F0.wireOp",EDGE,"E0.left");var subQ2=sQuery(id+"F19.wireOp",EDGE,"E23.right");Q1=makeQuery(id+"F28.boolean.opBoolean","COPY",EDGE,{"disambiguationData":[TD([makeQuery(id+"F2.opExtrude","SWEPT_FACE",FACE,{"disambiguationData":[OSD([subQ1])]})])],"derivedFrom":makeQuery(id+"F28.opExtrude","SWEPT_EDGE",EDGE,{"disambiguationData":[OSD([sQuery(id+"F19.wireOp",EDGE,"E23.bottom"),subQ2])]})});}
            var Q2;
            {var subQ1=sQuery(id+"F0.wireOp",EDGE,"E0.left");var subQ2=sQuery(id+"F19.wireOp",EDGE,"E24.MirrorCS");Q2=makeQuery(id+"F28.boolean.opBoolean","COPY",EDGE,{"disambiguationData":[TD([makeQuery(id+"F2.opExtrude","SWEPT_FACE",FACE,{"disambiguationData":[OSD([subQ1])]})])],"derivedFrom":makeQuery(id+"F28.opExtrude","SWEPT_EDGE",EDGE,{"disambiguationData":[OSD([subQ2,sQuery(id+"F19.wireOp",EDGE,"E26.MirrorCS")])]})});}
            var Q3;
            {var subQ1=sQuery(id+"F0.wireOp",EDGE,"E0.left");var subQ2=sQuery(id+"F19.wireOp",EDGE,"E25.MirrorCS");Q3=makeQuery(id+"F28.boolean.opBoolean","COPY",EDGE,{"disambiguationData":[TD([makeQuery(id+"F2.opExtrude","SWEPT_FACE",FACE,{"disambiguationData":[OSD([subQ1])]})])],"derivedFrom":makeQuery(id+"F28.opExtrude","SWEPT_EDGE",EDGE,{"disambiguationData":[OSD([subQ2,sQuery(id+"F19.wireOp",EDGE,"E26.MirrorCS")])]})});}
            var Q4;
            {var subQ1=sQuery(id+"F0.wireOp",EDGE,"E0.right");var subQ2=sQuery(id+"F19.wireOp",EDGE,"E25.MirrorCS");Q4=makeQuery(id+"F28.boolean.opBoolean","COPY",EDGE,{"disambiguationData":[TD([makeQuery(id+"F2.opExtrude","SWEPT_FACE",FACE,{"disambiguationData":[OSD([subQ1])]})])],"derivedFrom":makeQuery(id+"F28.opExtrude","SWEPT_EDGE",EDGE,{"disambiguationData":[OSD([subQ2,sQuery(id+"F19.wireOp",EDGE,"E26.MirrorCS")])]})});}
            var Q5;
            {var subQ1=sQuery(id+"F0.wireOp",EDGE,"E0.right");var subQ2=sQuery(id+"F19.wireOp",EDGE,"E24.MirrorCS");Q5=makeQuery(id+"F28.boolean.opBoolean","COPY",EDGE,{"disambiguationData":[TD([makeQuery(id+"F2.opExtrude","SWEPT_FACE",FACE,{"disambiguationData":[OSD([subQ1])]})])],"derivedFrom":makeQuery(id+"F28.opExtrude","SWEPT_EDGE",EDGE,{"disambiguationData":[OSD([subQ2,sQuery(id+"F19.wireOp",EDGE,"E26.MirrorCS")])]})});}
            var Q6;
            {var subQ1=sQuery(id+"F0.wireOp",EDGE,"E0.right");var subQ2=sQuery(id+"F19.wireOp",EDGE,"E23.right");Q6=makeQuery(id+"F28.boolean.opBoolean","COPY",EDGE,{"disambiguationData":[TD([makeQuery(id+"F2.opExtrude","SWEPT_FACE",FACE,{"disambiguationData":[OSD([subQ1])]})])],"derivedFrom":makeQuery(id+"F28.opExtrude","SWEPT_EDGE",EDGE,{"disambiguationData":[OSD([sQuery(id+"F19.wireOp",EDGE,"E23.bottom"),subQ2])]})});}
            var Q7;
            {var subQ1=sQuery(id+"F0.wireOp",EDGE,"E0.right");var subQ2=sQuery(id+"F19.wireOp",EDGE,"E23.left");Q7=makeQuery(id+"F28.boolean.opBoolean","COPY",EDGE,{"disambiguationData":[TD([makeQuery(id+"F2.opExtrude","SWEPT_FACE",FACE,{"disambiguationData":[OSD([subQ1])]})])],"derivedFrom":makeQuery(id+"F28.opExtrude","SWEPT_EDGE",EDGE,{"disambiguationData":[OSD([sQuery(id+"F19.wireOp",EDGE,"E23.bottom"),subQ2])]})});}
            fillet(context, id + "F29", {"entities" : qUnion([Q0, Q1, Q2, Q3, Q4, Q5, Q6, Q7]), "radius" : 5 * mm, "tangentPropagation" : true, "allowEdgeOverflow" : false});
        }
        {
            var Q0;
            Q0=makeQuery(id+"F2.opExtrude","CAP_EDGE",EDGE,{"disambiguationData":[OSD([sQuery(id+"F0.wireOp",EDGE,"E5.7")])],"isStart":false});
            chamfer(context, id + "F30", {"entities" : qUnion([Q0]), "width" : 0.6 * mm, "tangentPropagation" : true});
        }
        {
            var Q0;
            {var subQ0=sQuery(id+"F0.wireOp",EDGE,"E5.2");Q0=makeQuery(id+"F28.boolean.opBoolean","SPLIT",EDGE,{"disambiguationData":[TD([makeQuery(id+"F28.opExtrude","SWEPT_FACE",FACE,{"disambiguationData":[OSD([sQuery(id+"F19.wireOp",EDGE,"E23.right")])]})])],"derivedFrom":makeQuery(id+"F2.opExtrude","CAP_EDGE",EDGE,{"disambiguationData":[OSD([subQ0])],"isStart":false})});}
            var Q1;
            {var subQ0=sQuery(id+"F0.wireOp",EDGE,"E5.4");var subQ1=sQuery(id+"F0.wireOp",EDGE,"E5.2");Q1=makeQuery(id+"F28.boolean.opBoolean","SPLIT",EDGE,{"disambiguationData":[TD([makeQuery(id+"F2.opExtrude","SWEPT_FACE",FACE,{"disambiguationData":[OSD([subQ0])]})])],"derivedFrom":makeQuery(id+"F2.opExtrude","CAP_EDGE",EDGE,{"disambiguationData":[OSD([subQ1])],"isStart":false})});}
            var Q2;
            {var subQ0=sQuery(id+"F0.wireOp",EDGE,"E5.2");var subQ1=sQuery(id+"F0.wireOp",EDGE,"E5.0");Q2=makeQuery(id+"F28.boolean.opBoolean","SPLIT",EDGE,{"disambiguationData":[TD([makeQuery(id+"F2.opExtrude","SWEPT_FACE",FACE,{"disambiguationData":[OSD([subQ1])]})])],"derivedFrom":makeQuery(id+"F2.opExtrude","CAP_EDGE",EDGE,{"disambiguationData":[OSD([subQ0])],"isStart":false})});}
            chamfer(context, id + "F31", {"entities" : qUnion([Q0, Q1, Q2]), "width" : 0.6 * mm, "tangentPropagation" : true});
        }
        {
            var Q0;
            {var subQ1=sQuery(id+"F0.wireOp",EDGE,"E6.6");var subQ8=sQuery(id+"F0.wireOp",EDGE,"E6.7");var subQ9=sQuery(id+"F0.wireOp",EDGE,"E6.3");var subQ12=sQuery(id+"F0.wireOp",EDGE,"E6.4");var subQ14=sQuery(id+"F0.wireOp",EDGE,"E6.5");var subQ15=sQuery(id+"F0.wireOp",EDGE,"E6.2");var subQ16=sQuery(id+"F0.wireOp",EDGE,"E6.1");var subQ17=sQuery(id+"F0.wireOp",EDGE,"E6.0");var subQ18=sQuery(id+"F0.wireOp",EDGE,"E4.filletArc");var subQ19=sQuery(id+"F0.wireOp",EDGE,"E3.filletArc");var subQ20=sQuery(id+"F0.wireOp",EDGE,"E2.filletArc");var subQ21=sQuery(id+"F0.wireOp",EDGE,"E1.filletArc");var subQ22=sQuery(id+"F0.wireOp",EDGE,"E0.top");var subQ23=sQuery(id+"F0.wireOp",EDGE,"E0.bottom");var subQ24=makeQuery(id+"F3.opExtrude","CAP_FACE",FACE,{"disambiguationData":[OSD([subQ23,subQ22,sQuery(id+"F0.wireOp",EDGE,"E0.left"),sQuery(id+"F0.wireOp",EDGE,"E0.right"),subQ21,subQ20,subQ19,subQ18,subQ17,subQ16,subQ15,subQ9,subQ12,subQ14,subQ1,subQ8])],"isStart":false});var subQ38=subQ24;Q0=makeQuery(id+"F31.opChamfer","MERGE",FACE,{"derivedFrom":[makeQuery(id+"F15.boolean.opBoolean","SPLIT",FACE,{"disambiguationData":[TD([makeQuery(id+"F1.opExtrude","SWEPT_FACE",FACE,{"disambiguationData":[OSD([subQ17])]})])],"derivedFrom":subQ38}),makeQuery(id+"F15.boolean.opBoolean","SPLIT",FACE,{"disambiguationData":[TD([makeQuery(id+"F1.opExtrude","SWEPT_FACE",FACE,{"disambiguationData":[OSD([subQ14])]})])],"derivedFrom":subQ38})]});}
            var sketch = newSketch(context, id + "F32", { "sketchPlane" : qUnion([Q0])});
            skArc(sketch, "E35.0", {"start": v(0, -20.1) * mm, "mid": v(4.16, -20.5) * mm, "end": v(8.17, -21.71) * mm});
            skArc(sketch, "E35.1", {"start": v(-8.17, -21.71) * mm, "mid": v(-4.16, -20.5) * mm, "end": v(0, -20.1) * mm});
            skLineSegment(sketch, "E36", {"start": v(-8.17, -21.71) * mm, "end": v(-7.6, -23.1) * mm});
            skLineSegment(sketch, "E37", {"start": v(8.17, -21.71) * mm, "end": v(7.6, -23.1) * mm});
            skArc(sketch, "E38.0", {"start": v(0, 20.1) * mm, "mid": v(4.16, 20.5) * mm, "end": v(8.17, 21.71) * mm});
            skArc(sketch, "E38.1", {"start": v(-8.17, 21.71) * mm, "mid": v(-4.16, 20.5) * mm, "end": v(0, 20.1) * mm});
            skLineSegment(sketch, "E39", {"start": v(8.17, 21.71) * mm, "end": v(7.6, 23.1) * mm});
            skLineSegment(sketch, "E40", {"start": v(-8.17, 21.71) * mm, "end": v(-7.6, 23.1) * mm});
            skLineSegment(sketch, "E41", {"start": v(-7.6, -23.1) * mm, "end": v(7.6, -23.1) * mm});
            skLineSegment(sketch, "E42", {"start": v(-7.6, 23.1) * mm, "end": v(7.6, 23.1) * mm});
            skSolve(sketch);
        }
        {
            var Q0;
            {var subQ42=sQuery(id+"F32.wireOp",EDGE,"E38.1");var subQ43=sQuery(id+"F32.wireOp",EDGE,"E38.0");var subQ44=makeQuery(id+"F32.imprint","INTERSECT",VERTEX,{"derivedFrom":[subQ43,subQ42]});Q0=makeQuery(id+"F32.imprint","IMPRINT",FACE,{"disambiguationData":[TD([[makeQuery(id+"F32.imprint","IMPRINT",EDGE,{"disambiguationData":[TD([[subQ44,-1.0]])],"derivedFrom":subQ43}),1.0]])]});}
            var Q1;
            {var subQ43=sQuery(id+"F32.wireOp",EDGE,"E35.1");var subQ44=sQuery(id+"F32.wireOp",EDGE,"E35.0");var subQ45=makeQuery(id+"F32.imprint","INTERSECT",VERTEX,{"derivedFrom":[subQ44,subQ43]});Q1=makeQuery(id+"F32.imprint","IMPRINT",FACE,{"disambiguationData":[TD([[makeQuery(id+"F32.imprint","IMPRINT",EDGE,{"disambiguationData":[TD([[subQ45,-1.0]])],"derivedFrom":subQ44}),-1.0]])]});}
            extrude(context, id + "F33", {"entities" : qUnion([Q0, Q1]), "operationType" : NewBodyOperationType.REMOVE, "endBound" : BoundingType.THROUGH_ALL, "depth" : 25 * mm, "offsetDistance" : 25 * mm});
        }
        {
            var Q0;
            Q0=makeQuery(id+"F2.opExtrude","CAP_EDGE",EDGE,{"disambiguationData":[OSD([sQuery(id+"F0.wireOp",EDGE,"E7.right")])],"isStart":false});
            var Q1;
            Q1=makeQuery(id+"F2.opExtrude","CAP_EDGE",EDGE,{"disambiguationData":[OSD([sQuery(id+"F0.wireOp",EDGE,"E8.MirrorCS")])],"isStart":false});
            var Q2;
            Q2=makeQuery(id+"F2.opExtrude","CAP_EDGE",EDGE,{"disambiguationData":[OSD([sQuery(id+"F0.wireOp",EDGE,"E12.MirrorCS")])],"isStart":false});
            var Q3;
            Q3=makeQuery(id+"F2.opExtrude","CAP_EDGE",EDGE,{"disambiguationData":[OSD([sQuery(id+"F0.wireOp",EDGE,"E15.MirrorCS")])],"isStart":false});
            chamfer(context, id + "F34", {"entities" : qUnion([Q0, Q1, Q2, Q3]), "width" : 1 * mm});
        }
    });
